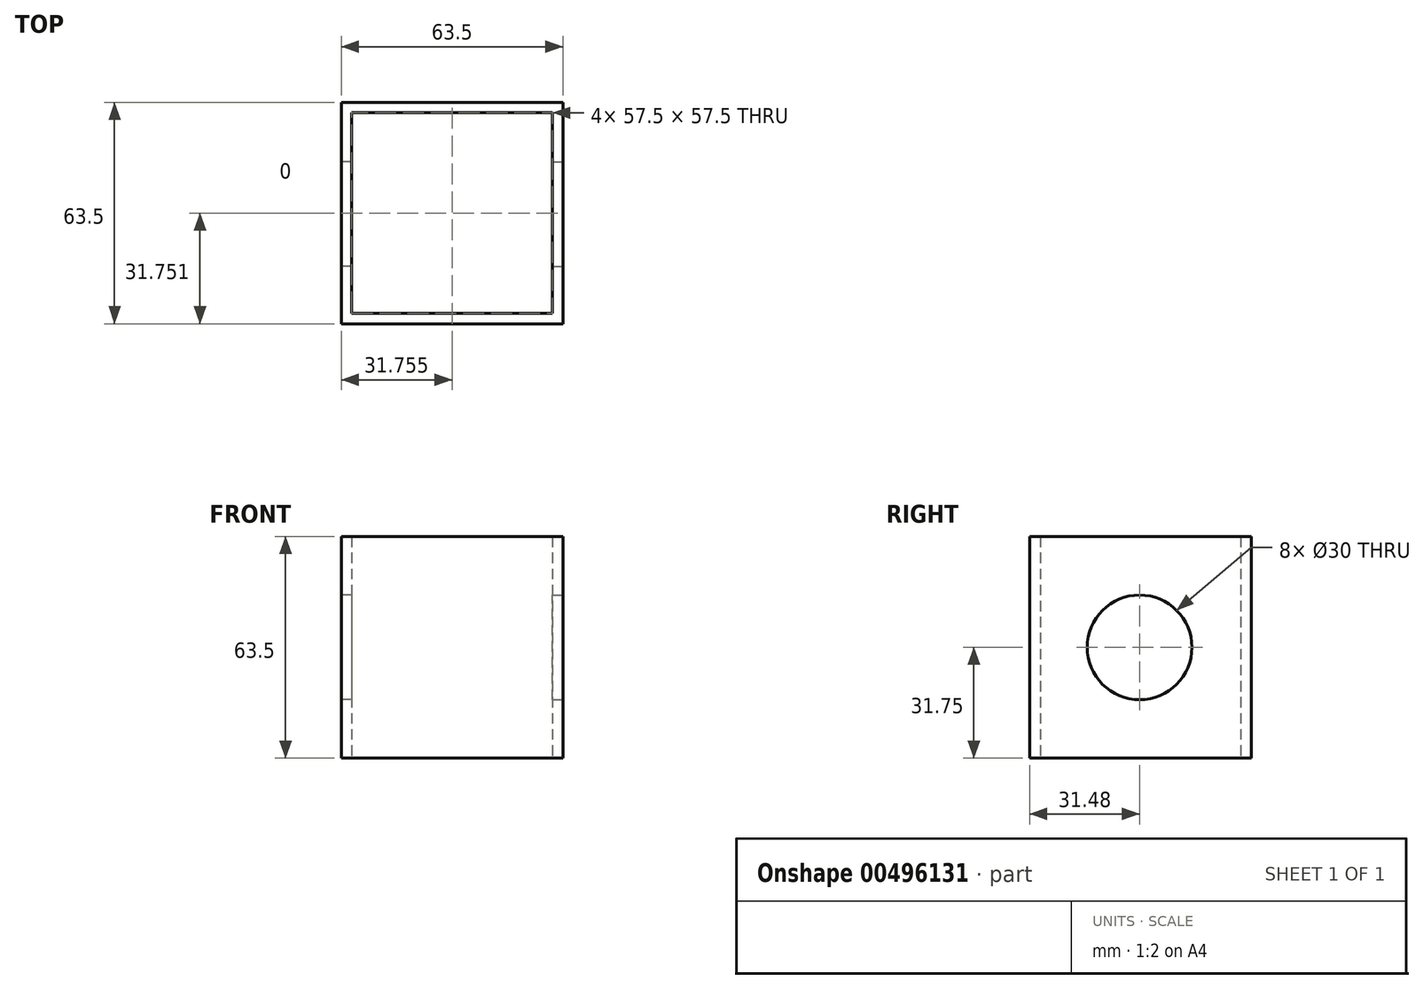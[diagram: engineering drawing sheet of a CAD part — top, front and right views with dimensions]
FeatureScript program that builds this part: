
annotation { "Feature Type Name" : "Feature", "Feature Type Description" : "" }
export const myFeature = defineFeature(function(context is Context, id is Id, definition is map)
    precondition{}
    {
        {
            var Q0;
            Q0=qCreatedBy(makeId("Top.planeOp"),FACE);
            var sketch = newSketch(context, id + "F0", { "sketchPlane" : qUnion([Q0])});
            skLineSegment(sketch, "E0.bottom", {"start": v(-28.45, 29.02) * mm, "end": v(29.05, 29.02) * mm});
            skLineSegment(sketch, "E0.top", {"start": v(-28.45, -28.48) * mm, "end": v(29.05, -28.48) * mm});
            skLineSegment(sketch, "E0.left", {"start": v(-28.45, 29.02) * mm, "end": v(-28.45, -28.48) * mm});
            skLineSegment(sketch, "E0.right", {"start": v(29.05, 29.02) * mm, "end": v(29.05, -28.48) * mm});
            skLineSegment(sketch, "E1.bottom", {"start": v(-31.45, 32.02) * mm, "end": v(32.05, 32.02) * mm});
            skLineSegment(sketch, "E1.top", {"start": v(-31.45, -31.48) * mm, "end": v(32.05, -31.48) * mm});
            skLineSegment(sketch, "E1.left", {"start": v(-31.45, 32.02) * mm, "end": v(-31.45, -31.48) * mm});
            skLineSegment(sketch, "E1.right", {"start": v(32.05, 32.02) * mm, "end": v(32.05, -31.48) * mm});
            skSolve(sketch);
        }
        {
            var Q0;
            Q0=qSketchRegion(id+"F0",true);
            extrude(context, id + "F1", {"entities" : qUnion([Q0]), "depth" : 63.5 * mm});
        }
        {
            var Q0;
            Q0=makeQuery(id+"F1.opExtrude","SWEPT_FACE",FACE,{"disambiguationData":[OSD([sQuery(id+"F0.wireOp",EDGE,"E1.right")])]});
            var sketch = newSketch(context, id + "F2", { "sketchPlane" : qUnion([Q0])});
            skLineSegment(sketch, "E2", {"start": v(0.24, 31.51) * mm, "end": v(0, 31.75) * mm});
            skCircle(sketch, "E3", {"center": v(0, 31.75) * mm, "radius": 15 * mm});
            skSolve(sketch);
        }
        {
            var Q0;
            Q0=qSketchRegion(id+"F2",true);
            extrude(context, id + "F3", {"entities" : qUnion([Q0]), "operationType" : NewBodyOperationType.REMOVE, "oppositeDirection" : true, "depth" : 3 * mm});
        }
        {
            var Q0;
            Q0=makeQuery(id+"F1.opExtrude","SWEPT_FACE",FACE,{"disambiguationData":[OSD([sQuery(id+"F0.wireOp",EDGE,"E1.left")])]});
            var sketch = newSketch(context, id + "F4", { "sketchPlane" : qUnion([Q0])});
            skCircle(sketch, "E4", {"center": v(0, 31.75) * mm, "radius": 15 * mm});
            skSolve(sketch);
        }
        {
            var Q0;
            Q0=qSketchRegion(id+"F4",true);
            extrude(context, id + "F5", {"entities" : qUnion([Q0]), "operationType" : NewBodyOperationType.REMOVE, "oppositeDirection" : true, "depth" : 3 * mm});
        }
    });
